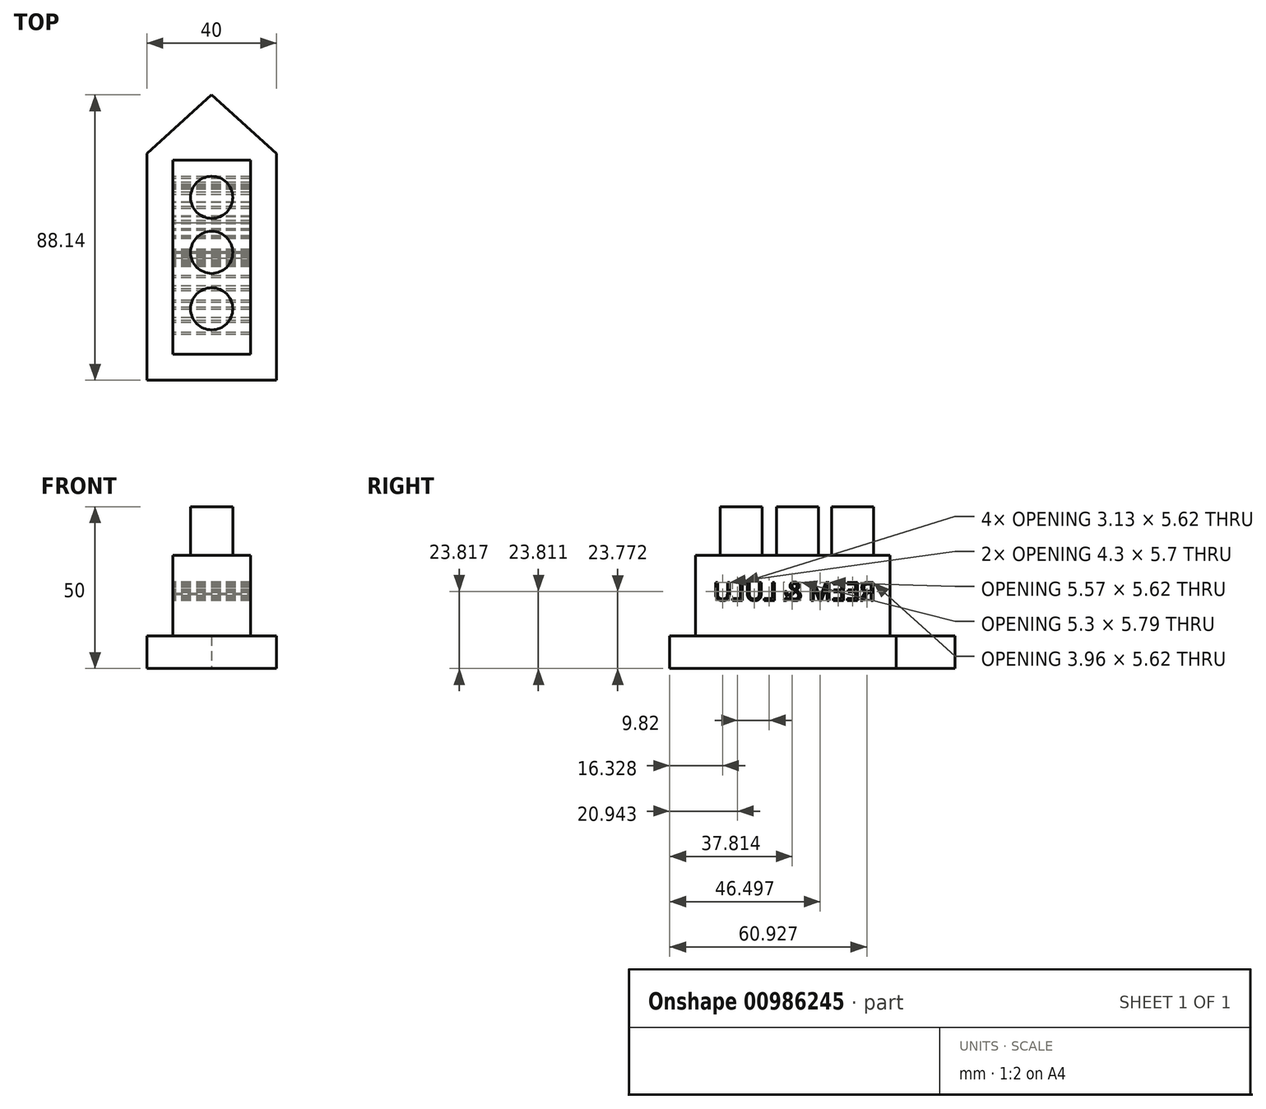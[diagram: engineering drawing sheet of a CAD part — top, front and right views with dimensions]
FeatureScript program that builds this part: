
annotation { "Feature Type Name" : "Feature", "Feature Type Description" : "" }
export const myFeature = defineFeature(function(context is Context, id is Id, definition is map)
    precondition{}
    {
        {
            var Q0;
            Q0=qCreatedBy(makeId("Top.planeOp"),FACE);
            var sketch = newSketch(context, id + "F0", { "sketchPlane" : qUnion([Q0])});
            skLineSegment(sketch, "E0", {"start": v(-20, 47.92) * mm, "end": v(-20, -22.08) * mm});
            skLineSegment(sketch, "E1", {"start": v(-20, 47.92) * mm, "end": v(0, 66.06) * mm});
            skLineSegment(sketch, "E2", {"start": v(0, 66.06) * mm, "end": v(20, 47.92) * mm});
            skLineSegment(sketch, "E3", {"start": v(20, 47.92) * mm, "end": v(20, -22.08) * mm});
            skLineSegment(sketch, "E4", {"start": v(20, -22.08) * mm, "end": v(-20, -22.08) * mm});
            skSolve(sketch);
        }
        {
            var Q0;
            Q0 = qSketchRegion(id + "F0", true);
            extrude(context, id + "F1", {"entities" : qUnion([Q0]), "depth" : 10 * mm, "offsetDistance" : 25 * mm});
        }
        {
            var Q0;
            Q0=makeQuery(id+"F1.opExtrude","CAP_FACE",FACE,{"disambiguationData":[OSD([sQuery(id+"F0.wireOp",EDGE,"E0"),sQuery(id+"F0.wireOp",EDGE,"E1"),sQuery(id+"F0.wireOp",EDGE,"E2"),sQuery(id+"F0.wireOp",EDGE,"E3"),sQuery(id+"F0.wireOp",EDGE,"E4")])],"isStart":false});
            var sketch = newSketch(context, id + "F2", { "sketchPlane" : qUnion([Q0])});
            skLineSegment(sketch, "E5.bottom", {"start": v(-12, 45.92) * mm, "end": v(12, 45.92) * mm});
            skLineSegment(sketch, "E5.top", {"start": v(-12, -14.08) * mm, "end": v(12, -14.08) * mm});
            skLineSegment(sketch, "E5.left", {"start": v(-12, 45.92) * mm, "end": v(-12, -14.08) * mm});
            skLineSegment(sketch, "E5.right", {"start": v(12, 45.92) * mm, "end": v(12, -14.08) * mm});
            skSolve(sketch);
        }
        {
            var Q0;
            Q0 = qSketchRegion(id + "F2", true);
            extrude(context, id + "F3", {"entities" : qUnion([Q0]), "operationType" : NewBodyOperationType.ADD, "depth" : 25 * mm, "offsetDistance" : 25 * mm});
        }
        {
            var Q0;
            Q0=makeQuery(id+"F3.opExtrude","CAP_FACE",FACE,{"disambiguationData":[OSD([sQuery(id+"F2.wireOp",EDGE,"E5.bottom"),sQuery(id+"F2.wireOp",EDGE,"E5.top"),sQuery(id+"F2.wireOp",EDGE,"E5.left"),sQuery(id+"F2.wireOp",EDGE,"E5.right")])],"isStart":false});
            var sketch = newSketch(context, id + "F4", { "sketchPlane" : qUnion([Q0])});
            skCircle(sketch, "E6", {"center": v(0, 34.42) * mm, "radius": 6.5 * mm});
            skCircle(sketch, "E7", {"center": v(0, 17.42) * mm, "radius": 6.5 * mm});
            skCircle(sketch, "E8", {"center": v(0, 0) * mm, "radius": 6.5 * mm});
            skSolve(sketch);
        }
        {
            var Q0;
            Q0 = qSketchRegion(id + "F4", true);
            extrude(context, id + "F5", {"entities" : qUnion([Q0]), "operationType" : NewBodyOperationType.ADD, "depth" : 15 * mm, "offsetDistance" : 25 * mm});
        }
        {
            var Q0;
            Q0=makeQuery(id+"F3.opExtrude","SWEPT_FACE",FACE,{"disambiguationData":[OSD([sQuery(id+"F2.wireOp",EDGE,"E5.left")])]});
            var sketch = newSketch(context, id + "F6", { "sketchPlane" : qUnion([Q0])});
            skText(sketch, "E9", { "text": "REEM & LULU", "fontName": "OpenSans-Regular.ttf"});
            const initialGuessF6  = {"E9": [-0.0416, 0.021, 1, 0, 0.00567]};
            skSetInitialGuess(sketch, initialGuessF6);
            skSolve(sketch);
        }
        {
            var Q0;
            Q0 = qSketchRegion(id + "F6", true);
            extrude(context, id + "F7", {"entities" : qUnion([Q0]), "operationType" : NewBodyOperationType.REMOVE, "oppositeDirection" : true, "depth" : 25 * mm, "offsetDistance" : 25 * mm});
        }
    });
